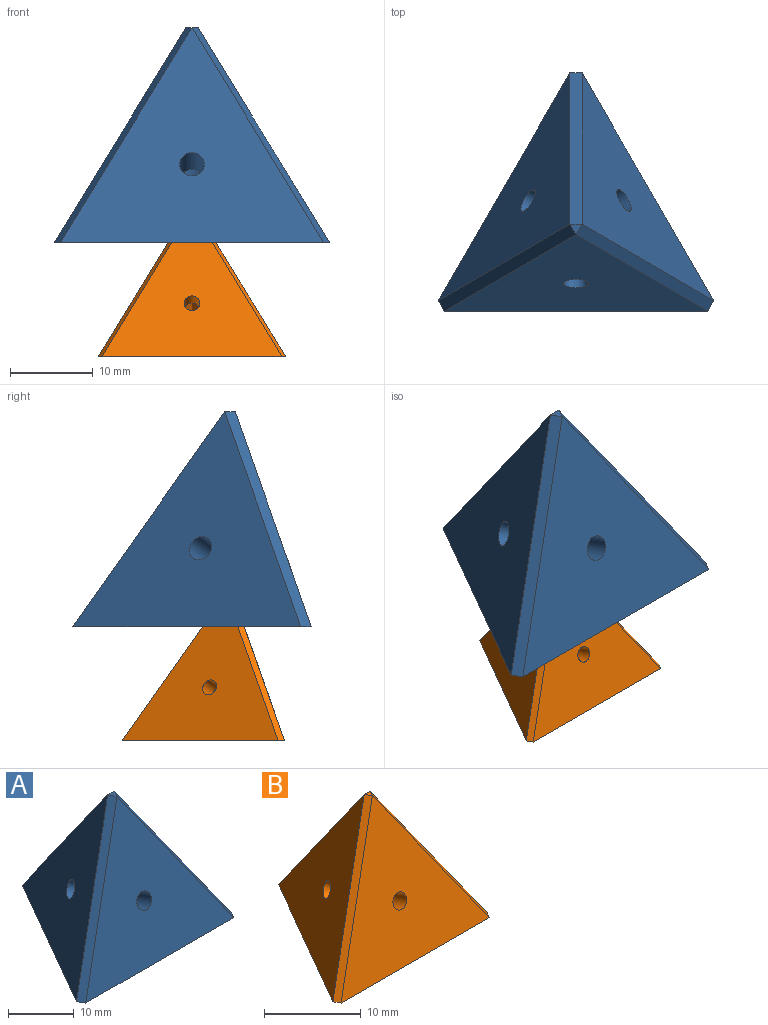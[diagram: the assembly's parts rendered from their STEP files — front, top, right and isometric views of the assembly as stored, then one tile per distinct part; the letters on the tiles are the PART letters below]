
ASSEMBLY  parts=2 mates=1
PART A: 21 faces, bbox 33.2x28.7x25.9 mm
  f0: plane 27.47x25.9mm, normal (-0.82,0.47,0.33), area 428.6mm2, adj f3,f12,f13,f14
  f1: plane 31.72x25.9mm, normal (0,-0.94,0.33), area 428.6mm2, adj f3,f8,f13,f16
  f2: plane 27.47x25.9mm, normal (0.82,0.47,0.33), area 428.6mm2, adj f3,f10,f14,f16
  f3: plane 33.19x28.74mm, normal (0,0,-1), area 499mm2, adj f0,f1,f2,f4,f5,f6,f13,f14
  f4: plane 4.24x4mm, normal (0.82,-0.47,-0.33), area 10.4mm2, adj f3,f18,f20
  f5: plane 4.9x4mm, normal (0,0.94,-0.33), area 10.4mm2, adj f3,f17,f20
  f6: plane 4.24x4mm, normal (-0.82,-0.47,-0.33), area 10.4mm2, adj f3,f17,f18
  f7: cone r=0mm half-angle=59deg, axis (0,-0.94,0.33), area 7mm2, adj f8,f9,f11
  f8: cylinder r=1.5mm len=6.75mm, axis (0,-0.94,0.33), area 57.5mm2, adj f1,f7,f10,f12
  f9: cone r=0mm half-angle=59deg, axis (0.82,0.47,0.33), area 7mm2, adj f7,f10,f11
  f10: cylinder r=1.5mm len=6.71mm, axis (0.82,0.47,0.33), area 57.5mm2, adj f2,f8,f9,f12
  f11: cone r=0mm half-angle=59deg, axis (-0.82,0.47,0.33), area 7mm2, adj f7,f9,f12
  f12: cylinder r=1.5mm len=6.71mm, axis (-0.82,0.47,0.33), area 57.5mm2, adj f0,f8,f10,f11
  f13: plane 25.9x16.59mm, normal (-0.71,-0.41,0.58), area 46.5mm2, adj f0,f1,f3,f15
  f14: plane 25.9x18.31mm, normal (0,0.82,0.58), area 46.5mm2, adj f0,f2,f3,f15
  f15: plane 1.47x1.27mm, normal (0,0,1), area 0.9mm2, adj f13,f14,f16
  f16: plane 25.9x16.59mm, normal (0.71,-0.41,0.58), area 46.5mm2, adj f1,f2,f3,f15
  f17: plane 4x2.89mm, normal (-0.71,0.41,-0.58), area 4.3mm2, adj f3,f5,f6,f19
  f18: plane 4x2.83mm, normal (0,-0.82,-0.58), area 4.3mm2, adj f3,f4,f6,f19
  f19: plane 0.88x0.76mm, normal (0,0,-1), area 0.3mm2, adj f17,f18,f20
  f20: plane 4x2.89mm, normal (0.71,0.41,-0.58), area 4.3mm2, adj f3,f4,f5,f19
PART B: 14 faces, bbox 22.6x19.6x17.7 mm
  f0: plane 18.8x17.72mm, normal (-0.82,0.47,0.33), area 201.1mm2, adj f3,f9,f10,f13
  f1: plane 21.7x17.72mm, normal (0,-0.94,0.33), area 201.1mm2, adj f3,f8,f11,f13
  f2: plane 18.8x17.72mm, normal (0.82,0.47,0.33), area 201.1mm2, adj f3,f7,f10,f11
  f3: plane 22.58x19.56mm, normal (0,0,-1), area 150.9mm2, adj f0,f1,f2,f4,f5,f6,f10,f11
  f4: plane 12.24x11.54mm, normal (0.82,-0.47,-0.33), area 83.6mm2, adj f3,f5,f6,f9
  f5: plane 14.13x11.54mm, normal (0,0.94,-0.33), area 83.6mm2, adj f3,f4,f6,f8
  f6: plane 12.24x11.54mm, normal (-0.82,-0.47,-0.33), area 83.6mm2, adj f3,f4,f5,f7
  f7: cylinder r=0.95mm len=3.17mm, axis (0.82,0.47,0.33), area 15.2mm2, adj f2,f6
  f8: cylinder r=0.95mm len=3.03mm, axis (0,-0.94,0.33), area 15.2mm2, adj f1,f5
  f9: cylinder r=0.95mm len=3.17mm, axis (-0.82,0.47,0.33), area 15.2mm2, adj f0,f4
  f10: plane 17.72x12.53mm, normal (0,0.82,0.58), area 19.1mm2, adj f0,f2,f3,f12
  f11: plane 17.72x11.29mm, normal (0.71,-0.41,0.58), area 19.1mm2, adj f1,f2,f3,f12
  f12: plane 0.88x0.76mm, normal (0,0,1), area 0.3mm2, adj f10,f11,f13
  f13: plane 17.72x11.29mm, normal (-0.71,-0.41,0.58), area 19.1mm2, adj f0,f1,f3,f12
PLACE A at identity
PLACE B t=(0,0,-13.72)mm
MATE planar B.f12 <-> A.f19  axis (0,0,1) through (0,0,4)mm
